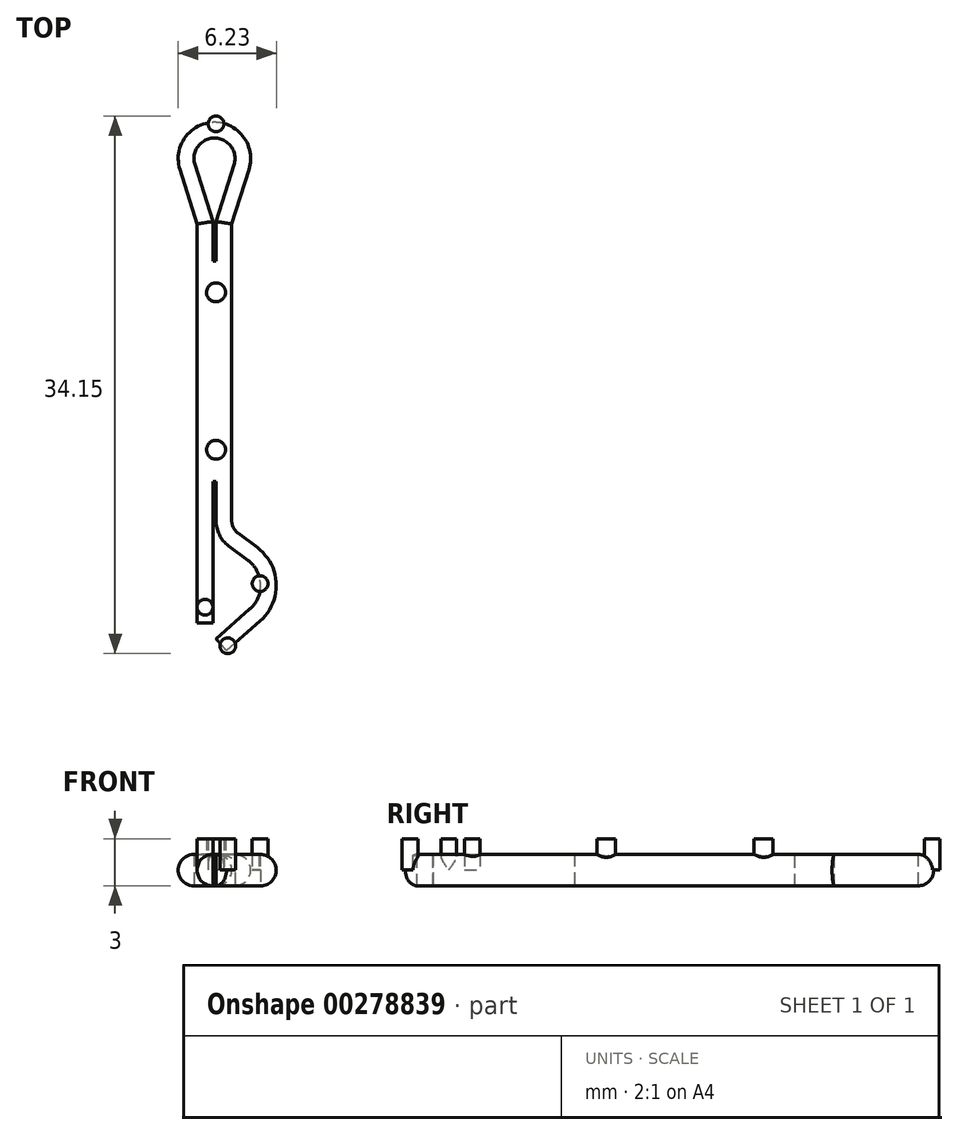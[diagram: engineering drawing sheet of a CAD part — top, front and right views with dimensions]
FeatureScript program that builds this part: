
annotation { "Feature Type Name" : "Feature", "Feature Type Description" : "" }
export const myFeature = defineFeature(function(context is Context, id is Id, definition is map)
    precondition{}
    {
        {
            var Q0;
            Q0=qCreatedBy(makeId("Top.planeOp"),FACE);
            var sketch = newSketch(context, id + "F0", { "sketchPlane" : qUnion([Q0])});
            skLineSegment(sketch, "E0", {"start": v(0, 1) * mm, "end": v(0, 20) * mm});
            skLineSegment(sketch, "E1", {"start": v(-0.2, 20) * mm, "end": v(-0.2, 0) * mm});
            skLineSegment(sketch, "E2", {"start": v(-0.2, 0) * mm, "end": v(-0.2, -5.5) * mm});
            skLineSegment(sketch, "E3", {"start": v(0.8, -0.6) * mm, "end": v(2.03, -1.52) * mm});
            skLineSegment(sketch, "E4", {"start": v(2.14, -4.62) * mm, "end": v(0, -6.5) * mm});
            skLineSegment(sketch, "E5", {"start": v(0, 20) * mm, "end": v(1.14, 23.6) * mm});
            skArc(sketch, "E6", {"start": v(1.14, 23.6) * mm, "mid": v(-0.1, 25.3) * mm, "end": v(-1.34, 23.6) * mm});
            skLineSegment(sketch, "E7", {"start": v(-1.34, 23.6) * mm, "end": v(-0.2, 20) * mm});
            skPoint(sketch, "E8.visualSharp", {"position": v(0, 0) * mm});
            skArc(sketch, "E8.filletArc", {"start": v(0, 1) * mm, "mid": v(0.21, 0.1) * mm, "end": v(0.8, -0.6) * mm});
            skPoint(sketch, "E9.visualSharp", {"position": v(4, -3) * mm});
            skArc(sketch, "E9.filletArc", {"start": v(2.14, -4.62) * mm, "mid": v(2.82, -3.04) * mm, "end": v(2.03, -1.52) * mm});
            skSolve(sketch);
        }
        {
            var Q0;
            Q0=sQuery(id+"F0.wireOp",VERTEX,"E2.end");
            var Q1;
            Q1=qCreatedBy(makeId("Front.planeOp"),FACE);
            cPlane(context, id + "F1", {"entities" : qUnion([Q0, Q1]), "cplaneType" : CPlaneType.PLANE_POINT, "offset" : 25 * mm, "width" : 150 * mm, "height" : 150 * mm});
        }
        {
            var Q0;
            Q0=qCreatedBy(id+"F1.planeOp",FACE);
            var sketch = newSketch(context, id + "F2", { "sketchPlane" : qUnion([Q0])});
            skArc(sketch, "E10", {"start": v(-0.2, 1) * mm, "mid": v(-1.2, 0) * mm, "end": v(-0.2, -1) * mm});
            skLineSegment(sketch, "E11", {"start": v(-0.2, 0) * mm, "end": v(-0.2, -1) * mm});
            skLineSegment(sketch, "E12", {"start": v(-0.2, 0) * mm, "end": v(-0.2, 1) * mm});
            skSolve(sketch);
        }
        {
            var Q0;
            Q0=makeQuery(id+"F2.imprint","IMPRINT",FACE,{"disambiguationData":[TD([[makeQuery(id+"F2.imprint","IMPRINT",EDGE,{"derivedFrom":sQuery(id+"F2.wireOp",EDGE,"E10")}),1.0]])]});
            var Q1;
            Q1 = qConstructionFilter(qBodyType(qCreatedBy(id + "F0" ,EDGE), BodyType.WIRE), ConstructionObject.NO);
            sweep(context, id + "F3", {"profiles" : qUnion([Q0]), "path" : qUnion([Q1])});
        }
        {
            var Q0;
            Q0=makeQuery(id+"F3.opSweep","SWEPT_FACE",FACE,{"disambiguationData":[OSD([sQuery(id+"F0.wireOp",EDGE,"E1"),sQuery(id+"F2.wireOp",EDGE,"E11"),sQuery(id+"F2.wireOp",EDGE,"E12")])]});
            var sketch = newSketch(context, id + "F4", { "sketchPlane" : qUnion([Q0])});
            skLineSegment(sketch, "E13.bottom", {"start": v(3.5, 1) * mm, "end": v(17.5, 1) * mm});
            skLineSegment(sketch, "E13.top", {"start": v(3.5, -1) * mm, "end": v(17.5, -1) * mm});
            skLineSegment(sketch, "E13.left", {"start": v(3.5, 1) * mm, "end": v(3.5, -1) * mm});
            skLineSegment(sketch, "E13.right", {"start": v(17.5, 1) * mm, "end": v(17.5, -1) * mm});
            skSolve(sketch);
        }
        {
            var Q0;
            Q0 = qSketchRegion(id + "F4", true);
            extrude(context, id + "F5", {"entities" : qUnion([Q0]), "operationType" : NewBodyOperationType.ADD, "endBound" : BoundingType.UP_TO_NEXT, "depth" : 25 * mm});
        }
        {
            var Q0;
            Q0=qCreatedBy(makeId("Top.planeOp"),FACE);
            var sketch = newSketch(context, id + "F6", { "sketchPlane" : qUnion([Q0])});
            skCircle(sketch, "E14", {"center": v(0, 15.5) * mm, "radius": 0.6 * mm});
            skCircle(sketch, "E15", {"center": v(0, 5.5) * mm, "radius": 0.6 * mm});
            skCircle(sketch, "E16", {"center": v(0, 26.2) * mm, "radius": 0.5 * mm});
            skCircle(sketch, "E17", {"center": v(2.8, -3) * mm, "radius": 0.5 * mm});
            skCircle(sketch, "E18", {"center": v(-0.7, -4.5) * mm, "radius": 0.5 * mm});
            skCircle(sketch, "E19", {"center": v(0.75, -6.95) * mm, "radius": 0.5 * mm});
            skSolve(sketch);
        }
        {
            var Q0;
            Q0 = qSketchRegion(id + "F6", true);
            extrude(context, id + "F7", {"entities" : qUnion([Q0]), "operationType" : NewBodyOperationType.ADD, "depth" : 2 * mm});
        }
    });
